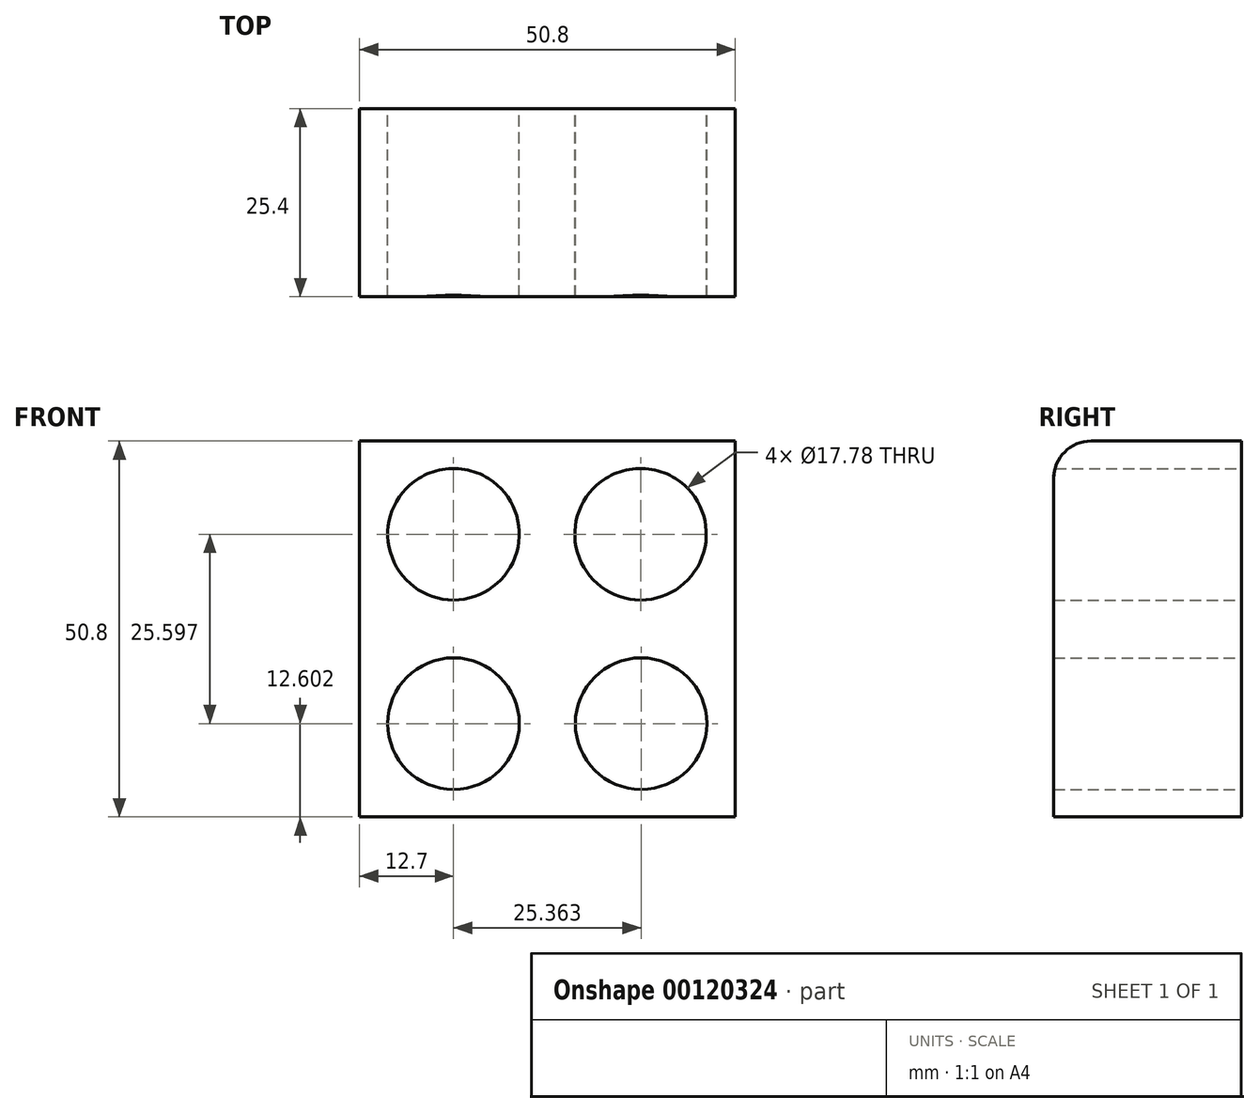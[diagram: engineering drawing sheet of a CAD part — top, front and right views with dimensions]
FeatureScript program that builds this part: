
annotation { "Feature Type Name" : "Feature", "Feature Type Description" : "" }
export const myFeature = defineFeature(function(context is Context, id is Id, definition is map)
    precondition{}
    {
        {
            var Q0;
            Q0=qCreatedBy(makeId("Front.planeOp"),FACE);
            var sketch = newSketch(context, id + "F0", { "sketchPlane" : qUnion([Q0])});
            skLineSegment(sketch, "E0.bottom", {"start": v(-25.4, 25.4) * mm, "end": v(25.4, 25.4) * mm});
            skLineSegment(sketch, "E0.top", {"start": v(-25.4, -25.4) * mm, "end": v(25.4, -25.4) * mm});
            skLineSegment(sketch, "E0.left", {"start": v(-25.4, 25.4) * mm, "end": v(-25.4, -25.4) * mm});
            skLineSegment(sketch, "E0.right", {"start": v(25.4, 25.4) * mm, "end": v(25.4, -25.4) * mm});
            skPoint(sketch, "E0.middle", {"position": v(0, 0) * mm});
            skLineSegment(sketch, "E1", {"start": v(0, 25.4) * mm, "end": v(0, -25.4) * mm});
            skLineSegment(sketch, "E2", {"start": v(-25.4, 0) * mm, "end": v(25.4, 0) * mm});
            skLineSegment(sketch, "E3", {"start": v(-25.4, 25.4) * mm, "end": v(-12.7, 25.4) * mm});
            skLineSegment(sketch, "E4", {"start": v(-12.7, 25.4) * mm, "end": v(-12.7, -25.4) * mm});
            skLineSegment(sketch, "E5", {"start": v(12.55, 25.4) * mm, "end": v(12.7, -25.4) * mm});
            skLineSegment(sketch, "E6", {"start": v(-25.4, 12.8) * mm, "end": v(25.4, 12.8) * mm});
            skLineSegment(sketch, "E7", {"start": v(-25.4, -12.8) * mm, "end": v(25.4, -12.8) * mm});
            skCircle(sketch, "E8", {"center": v(-12.7, 12.8) * mm, "radius": 8.9 * mm});
            skCircle(sketch, "E9", {"center": v(12.59, 12.8) * mm, "radius": 8.9 * mm});
            skCircle(sketch, "E10", {"center": v(12.66, -12.8) * mm, "radius": 8.9 * mm});
            skCircle(sketch, "E11", {"center": v(-12.7, -12.8) * mm, "radius": 8.9 * mm});
            skSolve(sketch);
        }
        {
            var Q0;
            Q0 = qSketchRegion(id + "F0", true);
            var Q1;
            {var subQ0=sQuery(id+"F0.wireOp",EDGE,"E6");var subQ1=sQuery(id+"F0.wireOp",EDGE,"E1");var subQ2=makeQuery(id+"F0.imprint","INTERSECT",VERTEX,{"derivedFrom":[subQ1,subQ0]});Q1=makeQuery(id+"F0.imprint","IMPRINT",FACE,{"disambiguationData":[TD([[makeQuery(id+"F0.imprint","IMPRINT",EDGE,{"disambiguationData":[TD([[subQ2,-1.0]])],"derivedFrom":subQ1}),1.0]])]});}
            var Q2;
            {var subQ1=sQuery(id+"F0.wireOp",EDGE,"E1");var subQ5=sQuery(id+"F0.wireOp",EDGE,"E2");var subQ6=makeQuery(id+"F0.imprint","INTERSECT",VERTEX,{"derivedFrom":[subQ1,subQ5]});Q2=makeQuery(id+"F0.imprint","IMPRINT",FACE,{"disambiguationData":[TD([[makeQuery(id+"F0.imprint","IMPRINT",EDGE,{"disambiguationData":[TD([[subQ6,-1.0]])],"derivedFrom":subQ1}),1.0]])]});}
            var Q3;
            {var subQ0=sQuery(id+"F0.wireOp",EDGE,"E6");var subQ1=sQuery(id+"F0.wireOp",EDGE,"E1");var subQ2=makeQuery(id+"F0.imprint","INTERSECT",VERTEX,{"derivedFrom":[subQ1,subQ0]});Q3=makeQuery(id+"F0.imprint","IMPRINT",FACE,{"disambiguationData":[TD([[makeQuery(id+"F0.imprint","IMPRINT",EDGE,{"disambiguationData":[TD([[subQ2,-1.0]])],"derivedFrom":subQ1}),-1.0]])]});}
            var Q4;
            {var subQ1=sQuery(id+"F0.wireOp",EDGE,"E2");var subQ6=sQuery(id+"F0.wireOp",EDGE,"E1");var subQ9=makeQuery(id+"F0.imprint","INTERSECT",VERTEX,{"derivedFrom":[subQ6,subQ1]});Q4=makeQuery(id+"F0.imprint","IMPRINT",FACE,{"disambiguationData":[TD([[makeQuery(id+"F0.imprint","IMPRINT",EDGE,{"disambiguationData":[TD([[subQ9,-1.0]])],"derivedFrom":subQ6}),-1.0]])]});}
            extrude(context, id + "F1", {"entities" : qUnion([Q0, Q1, Q2, Q3, Q4]), "depth" : 25.4 * mm});
        }
        {
            var Q0;
            Q0=makeQuery(id+"F1.opExtrude","CAP_EDGE",EDGE,{"disambiguationData":[OSD([sQuery(id+"F0.wireOp",EDGE,"E0.bottom"),sQuery(id+"F0.wireOp",EDGE,"E3")])],"isStart":false});
            fillet(context, id + "F2", {"entities" : qUnion([Q0]), "radius" : 5.08 * mm, "tangentPropagation" : true, "allowEdgeOverflow" : false});
        }
    });
